# Revit family: Hager-IC-IP40-Plain_Door-sistema-NoHosted-PT-pt
name_source: partatom
category: Electrical Equipment
units: mm (PartAtom-declared; Revit-internal decimal feet)

## family parameters
Always vertical = Yes
Cut with Voids When Loaded = No
Panel Configuration = Two Columns, Circuits Across
Part Type = Panelboard
Room Calculation Point = No
Round Connector Dimension = Use Diameter
Shared = No
Work Plane-Based = Yes

## types (4) — shared parameters
Default Elevation = 1219 mm
EF000116 - Número RAL = 9010
EF000118 - Com tampa de montagem = No
EF000266 - Número de linhas = 2
EF000339 - Tipo de difusor = EV004216 - Porta
EF001062 - Versão EMC = No
EF002950 - Largura em número de módulos = 12
EF005474 - Grau de proteção (IP) = EV006415 - IP40
EF006244 - Tampa/porta transparente = No
EF006306 - Com fecho = No
EF009212 - Tipo de tampa = EV000116 - Fechado
EF015776 - Borne de terra = Yes
EF015777 - Borne de neutro = Yes
EF015941 - Porta para passagem de sinal = Yes
HG000001 - Número de colunas = 1
HG000002 - Com porta ou tampa = Yes
HG000003 - Gama = IC
HG000005 - Espessura = 3 mm  [stored 0.00984252 ft]
HG000009 - Porta dupla = No
HG000010 - Portas assimétricas = No
HG000011 - Filas vazias desde da parte de baixo = No
HG000017 - Distância entre polos = 18 mm  [stored 0.0590551 ft]
Manufacturer = Hager
Type Comments = IC
zero-valued in all types: HG000007 - Número de colunas vazias, HG000008 - Número de filas vazias

## per-type parameters (varying)
| type | EF000003 - Método de montagem | EF000007 - Cor | EF000008 - Largura | EF000040 - Altura | EF000049 - Profundidade | EF000218 - Profundidade incorporada | EF000332 - Altura embutida | EF000846 - Largura para embutir | EF001088 - Extensão possível | EF001131 - Profundidade interior | EF001134 - Calha DIN | EF001596 - Material do corpo | EF004462 - Tipo de fecho | HG000004 - Referência do Fabricante | HG000006 - Encastrado | Model |
| Montagem em superfície IP40 L294 A326.5 P92.5 12 unidade de divisão - VD212PP | EV000384 - Montagem em superfície (gesso) | EV000202 - Branco | 294 mm | 326 mm | 92 mm | 0 mm  [stored 0 ft] | 0 mm  [stored 0 ft] | 0 mm  [stored 0 ft] | Yes | 72 mm  [stored 0.23622 ft] | Yes | EV000139 - Plástico | EV000154 - Outro | VD212PP | No | VD212PP |
| Montagem embutida IP40 L308 A351 P93 12 unidade de divisão - VR212PP | EV000383 - Montagem embutida (gesso) | EV000202 - Branco | 308 mm  [stored 1.0105 ft] | 351 mm  [stored 1.15157 ft] | 93 mm  [stored 0.305118 ft] | 72 mm  [stored 0.23622 ft] | 333 mm  [stored 1.09252 ft] | 290 mm  [stored 0.951444 ft] | Yes | 72 mm  [stored 0.23622 ft] | Yes | EV000139 - Plástico | EV000154 - Outro | VR212PP | Yes | VR212PP |
| Montagem embutida IP40 L308 A351 P93 12 unidade de divisão - VR212PPC | EV000383 - Montagem embutida (gesso) |  | 308 mm  [stored 1.0105 ft] | 351 mm  [stored 1.15157 ft] | 93 mm  [stored 0.305118 ft] | 72 mm  [stored 0.23622 ft] | 333 mm  [stored 1.09252 ft] | 290 mm  [stored 0.951444 ft] | No | 0 mm  [stored 0 ft] | No |  |  | VR212PPC | Yes | VR212PPC |
| Montagem embutida IP40 L308 A351 P93 12 unidade de divisão - VR212PPH | EV000383 - Montagem embutida (gesso) |  | 308 mm  [stored 1.0105 ft] | 351 mm  [stored 1.15157 ft] | 93 mm  [stored 0.305118 ft] | 72 mm  [stored 0.23622 ft] | 333 mm  [stored 1.09252 ft] | 290 mm  [stored 0.951444 ft] | No | 0 mm  [stored 0 ft] | No |  |  | VR212PPH | Yes | VR212PPH |

note: [stored X ft] marks values corroborated as IEEE doubles in the binary element streams (Revit-internal decimal feet)

## geometry (parser evidence)
native form markers: Sweep x13
no freeform markers — native parametric forms only
